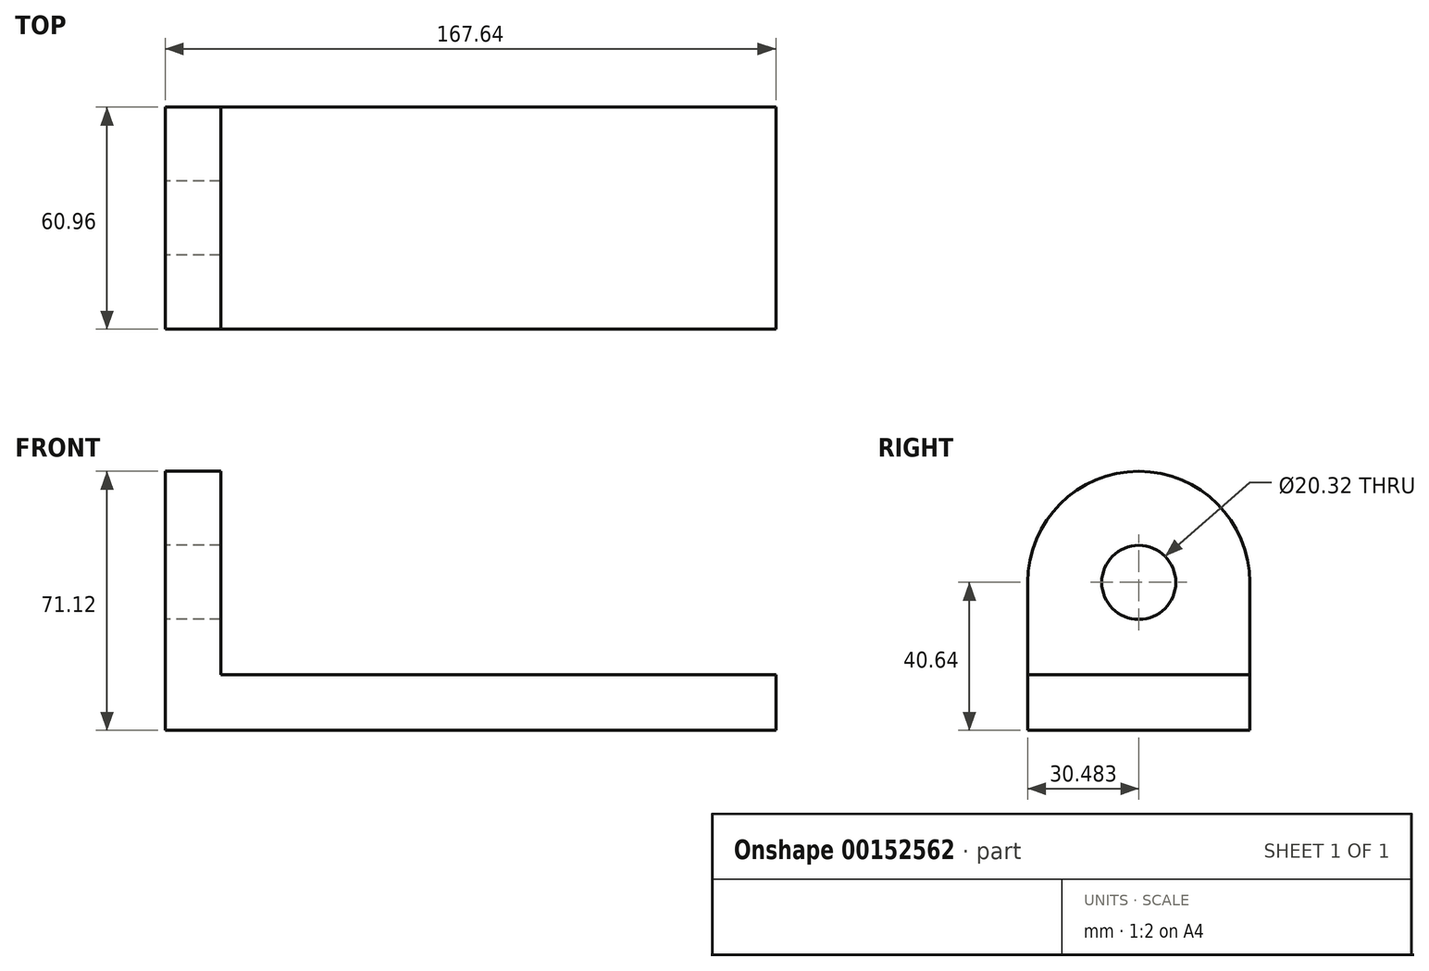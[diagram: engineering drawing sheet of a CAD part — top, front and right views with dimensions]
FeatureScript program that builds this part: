
annotation { "Feature Type Name" : "Feature", "Feature Type Description" : "" }
export const myFeature = defineFeature(function(context is Context, id is Id, definition is map)
    precondition{}
    {
        {
            var Q0;
            Q0=qCreatedBy(makeId("Top.planeOp"),FACE);
            var sketch = newSketch(context, id + "F0", { "sketchPlane" : qUnion([Q0])});
            skLineSegment(sketch, "E0.bottom", {"start": v(-33.03, -17.26) * mm, "end": v(134.61, -17.26) * mm});
            skLineSegment(sketch, "E0.top", {"start": v(-33.03, 43.7) * mm, "end": v(134.61, 43.7) * mm});
            skLineSegment(sketch, "E0.left", {"start": v(-33.03, -17.26) * mm, "end": v(-33.03, 43.7) * mm});
            skLineSegment(sketch, "E0.right", {"start": v(134.61, -17.26) * mm, "end": v(134.61, 43.7) * mm});
            skSolve(sketch);
        }
        {
            var Q0;
            Q0=makeQuery(id+"F0.imprint","IMPRINT",FACE,{"disambiguationData":[TD([[makeQuery(id+"F0.imprint","IMPRINT",EDGE,{"derivedFrom":sQuery(id+"F0.wireOp",EDGE,"E0.bottom")}),1.0]])]});
            extrude(context, id + "F1", {"entities" : qUnion([Q0]), "depth" : 15.24 * mm});
        }
        {
            var Q0;
            Q0=makeQuery(id+"F1.opExtrude","CAP_FACE",FACE,{"disambiguationData":[OSD([sQuery(id+"F0.wireOp",EDGE,"E0.bottom"),sQuery(id+"F0.wireOp",EDGE,"E0.top"),sQuery(id+"F0.wireOp",EDGE,"E0.left"),sQuery(id+"F0.wireOp",EDGE,"E0.right")])],"isStart":false});
            var sketch = newSketch(context, id + "F2", { "sketchPlane" : qUnion([Q0])});
            skLineSegment(sketch, "E1.bottom", {"start": v(-33.03, -17.26) * mm, "end": v(-17.79, -17.26) * mm});
            skLineSegment(sketch, "E1.top", {"start": v(-33.03, 43.7) * mm, "end": v(-17.79, 43.7) * mm});
            skLineSegment(sketch, "E1.left", {"start": v(-33.03, -17.26) * mm, "end": v(-33.03, 43.7) * mm});
            skLineSegment(sketch, "E1.right", {"start": v(-17.79, -17.26) * mm, "end": v(-17.79, 43.7) * mm});
            skSolve(sketch);
        }
        {
            var Q0;
            Q0 = qSketchRegion(id + "F2", true);
            extrude(context, id + "F3", {"entities" : qUnion([Q0]), "operationType" : NewBodyOperationType.ADD, "depth" : 55.88 * mm});
        }
        {
            var Q0;
            Q0=makeQuery(id+"F3.opExtrude","CAP_EDGE",EDGE,{"disambiguationData":[OSD([sQuery(id+"F2.wireOp",EDGE,"E1.bottom")])],"isStart":false});
            var Q1;
            Q1=makeQuery(id+"F3.opExtrude","CAP_EDGE",EDGE,{"disambiguationData":[OSD([sQuery(id+"F2.wireOp",EDGE,"E1.top")])],"isStart":false});
            fillet(context, id + "F4", {"entities" : qUnion([Q0, Q1]), "radius" : 30.48 * mm, "tangentPropagation" : true, "allowEdgeOverflow" : false});
        }
        {
            var Q0;
            Q0=makeQuery(id+"F3.boolean.opBoolean","MERGE",FACE,{"derivedFrom":[makeQuery(id+"F1.opExtrude","SWEPT_FACE",FACE,{"disambiguationData":[OSD([sQuery(id+"F0.wireOp",EDGE,"E0.left")])]}),makeQuery(id+"F3.opExtrude","SWEPT_FACE",FACE,{"disambiguationData":[OSD([sQuery(id+"F2.wireOp",EDGE,"E1.left")])]})]});
            var sketch = newSketch(context, id + "F5", { "sketchPlane" : qUnion([Q0])});
            skCircle(sketch, "E2", {"center": v(-13.22, 40.64) * mm, "radius": 10.16 * mm});
            skSolve(sketch);
        }
        {
            var Q0;
            Q0 = qSketchRegion(id + "F5", true);
            extrude(context, id + "F6", {"entities" : qUnion([Q0]), "operationType" : NewBodyOperationType.REMOVE, "oppositeDirection" : true, "depth" : 15.24 * mm});
        }
    });
